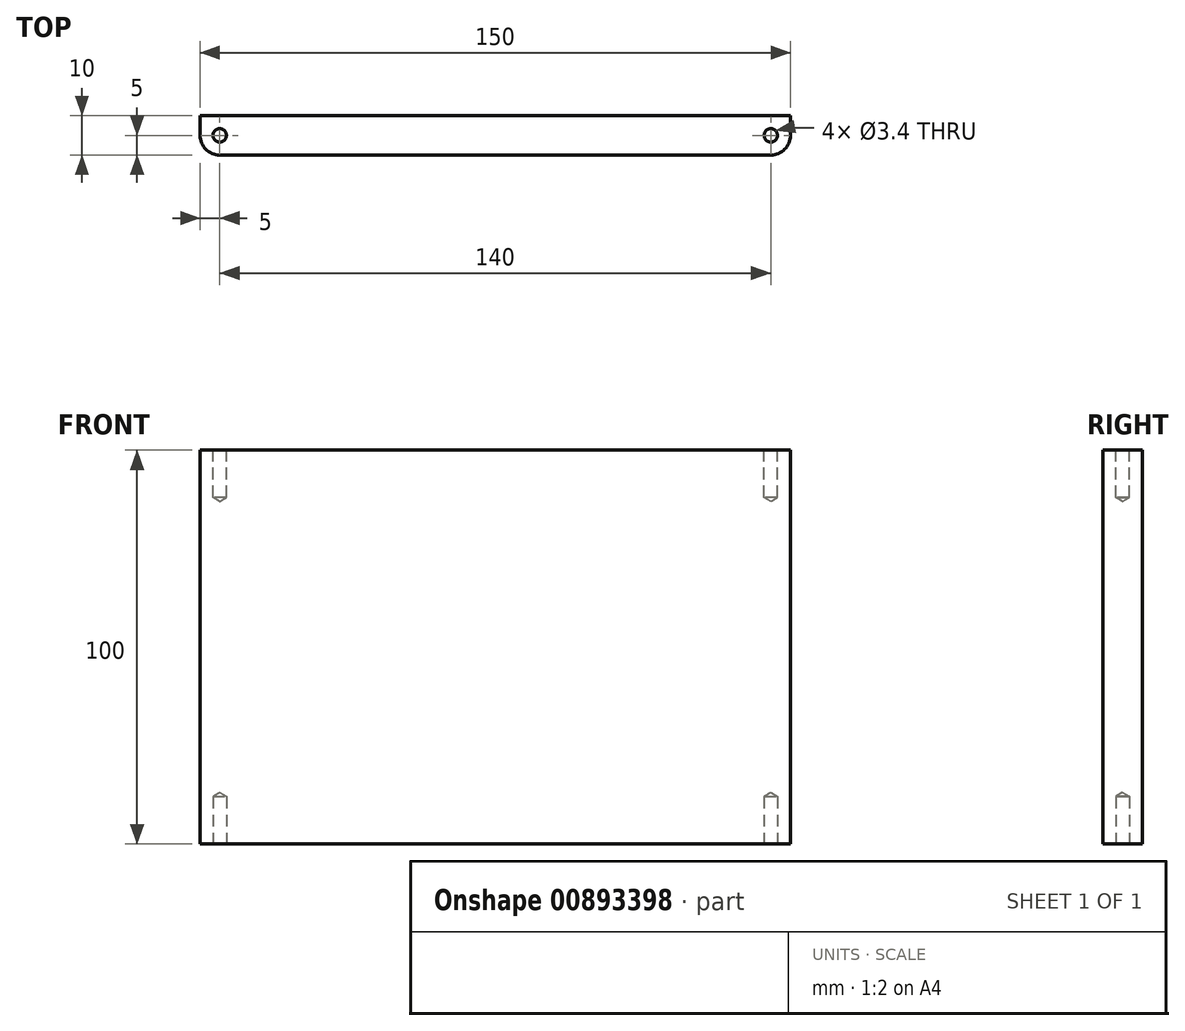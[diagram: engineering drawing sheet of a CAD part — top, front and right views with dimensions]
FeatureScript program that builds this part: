
annotation { "Feature Type Name" : "Feature", "Feature Type Description" : "" }
export const myFeature = defineFeature(function(context is Context, id is Id, definition is map)
    precondition{}
    {
        {
            var Q0;
            Q0=qCreatedBy(makeId("Front.planeOp"),FACE);
            var sketch = newSketch(context, id + "F0", { "sketchPlane" : qUnion([Q0])});
            skLineSegment(sketch, "E0.bottom", {"start": v(0, 0) * mm, "end": v(150, 0) * mm});
            skLineSegment(sketch, "E0.top", {"start": v(0, 100) * mm, "end": v(150, 100) * mm});
            skLineSegment(sketch, "E0.left", {"start": v(0, 0) * mm, "end": v(0, 100) * mm});
            skLineSegment(sketch, "E0.right", {"start": v(150, 0) * mm, "end": v(150, 100) * mm});
            skSolve(sketch);
        }
        {
            var Q0;
            Q0 = qSketchRegion(id + "F0", true);
            extrude(context, id + "F1", {"entities" : qUnion([Q0]), "depth" : 10 * mm, "offsetDistance" : 25 * mm});
        }
        {
            var Q0;
            Q0=makeQuery(id+"F1.opExtrude","SWEPT_FACE",FACE,{"disambiguationData":[OSD([sQuery(id+"F0.wireOp",EDGE,"E0.top")])]});
            var sketch = newSketch(context, id + "F2", { "sketchPlane" : qUnion([Q0])});
            skPoint(sketch, "E1", {"position": v(145, -5) * mm});
            skPoint(sketch, "E2", {"position": v(5, -5) * mm});
            skSolve(sketch);
        }
        {
            var Q0;
            Q0=sQuery(id+"F2.wireOp",VERTEX,"E1");
            var Q1;
            Q1=makeQuery(id+"F1.opExtrude","SWEPT_BODY",BODY,{"disambiguationData":[OSD([sQuery(id+"F0.wireOp",EDGE,"E0.bottom"),sQuery(id+"F0.wireOp",EDGE,"E0.top"),sQuery(id+"F0.wireOp",EDGE,"E0.left"),sQuery(id+"F0.wireOp",EDGE,"E0.right")])]});
            hole(context, id + "F3", {"style" : HoleStyle.SIMPLE, "endStyle" : HoleEndStyle.BLIND, "standardTappedOrClearance" : lookupTablePath({ "standard" : "ISO", "fit" : "Normal", "size" : "M3", "type" : "Clearance" }), "standardBlindInLast" : lookupTablePath({ "fit" : "Normal", "standard" : "ISO", "size" : "M3", "type" : "Clearance" }), "holeDiameter" : 3.4 * mm, "majorDiameter" : 5 * mm, "holeDepth" : 12 * mm, "isTappedThrough" : true, "tappedDepth" : 12 * mm, "tapClearance" : 3, "locations" : qUnion([Q0]), "scope" : qUnion([Q1])});
        }
        {
            var Q0;
            Q0=sQuery(id+"F2.wireOp",VERTEX,"E2");
            var Q1;
            Q1=makeQuery(id+"F1.opExtrude","SWEPT_BODY",BODY,{"disambiguationData":[OSD([sQuery(id+"F0.wireOp",EDGE,"E0.bottom"),sQuery(id+"F0.wireOp",EDGE,"E0.top"),sQuery(id+"F0.wireOp",EDGE,"E0.left"),sQuery(id+"F0.wireOp",EDGE,"E0.right")])]});
            hole(context, id + "F4", {"style" : HoleStyle.SIMPLE, "endStyle" : HoleEndStyle.BLIND, "standardTappedOrClearance" : lookupTablePath({ "standard" : "ISO", "fit" : "Normal", "size" : "M3", "type" : "Clearance" }), "standardBlindInLast" : lookupTablePath({ "fit" : "Normal", "standard" : "ISO", "size" : "M3", "type" : "Clearance" }), "holeDiameter" : 3.4 * mm, "majorDiameter" : 5 * mm, "holeDepth" : 12 * mm, "isTappedThrough" : true, "tappedDepth" : 12 * mm, "tapClearance" : 3, "locations" : qUnion([Q0]), "scope" : qUnion([Q1])});
        }
        {
            var Q0;
            Q0=makeQuery(id+"F1.opExtrude","SWEPT_FACE",FACE,{"disambiguationData":[OSD([sQuery(id+"F0.wireOp",EDGE,"E0.bottom")])]});
            var sketch = newSketch(context, id + "F5", { "sketchPlane" : qUnion([Q0])});
            skPoint(sketch, "E3", {"position": v(145, 5) * mm});
            skPoint(sketch, "E4", {"position": v(5, 5) * mm});
            skSolve(sketch);
        }
        {
            var Q0;
            Q0=sQuery(id+"F5.wireOp",VERTEX,"E3");
            var Q1;
            Q1=makeQuery(id+"F1.opExtrude","SWEPT_BODY",BODY,{"disambiguationData":[OSD([sQuery(id+"F0.wireOp",EDGE,"E0.bottom"),sQuery(id+"F0.wireOp",EDGE,"E0.top"),sQuery(id+"F0.wireOp",EDGE,"E0.left"),sQuery(id+"F0.wireOp",EDGE,"E0.right")])]});
            hole(context, id + "F6", {"style" : HoleStyle.SIMPLE, "endStyle" : HoleEndStyle.BLIND, "standardTappedOrClearance" : lookupTablePath({ "standard" : "ISO", "fit" : "Normal", "size" : "M3", "type" : "Clearance" }), "standardBlindInLast" : lookupTablePath({ "fit" : "Normal", "standard" : "ISO", "size" : "M3", "type" : "Clearance" }), "holeDiameter" : 3.4 * mm, "majorDiameter" : 5 * mm, "holeDepth" : 12 * mm, "isTappedThrough" : true, "tappedDepth" : 12 * mm, "tapClearance" : 3, "locations" : qUnion([Q0]), "scope" : qUnion([Q1])});
        }
        {
            var Q0;
            Q0=sQuery(id+"F5.wireOp",VERTEX,"E4");
            var Q1;
            Q1=makeQuery(id+"F1.opExtrude","SWEPT_BODY",BODY,{"disambiguationData":[OSD([sQuery(id+"F0.wireOp",EDGE,"E0.bottom"),sQuery(id+"F0.wireOp",EDGE,"E0.top"),sQuery(id+"F0.wireOp",EDGE,"E0.left"),sQuery(id+"F0.wireOp",EDGE,"E0.right")])]});
            hole(context, id + "F7", {"style" : HoleStyle.SIMPLE, "endStyle" : HoleEndStyle.BLIND, "standardTappedOrClearance" : lookupTablePath({ "standard" : "ISO", "fit" : "Normal", "size" : "M3", "type" : "Clearance" }), "standardBlindInLast" : lookupTablePath({ "fit" : "Normal", "standard" : "ISO", "size" : "M3", "type" : "Clearance" }), "holeDiameter" : 3.4 * mm, "majorDiameter" : 5 * mm, "holeDepth" : 12 * mm, "isTappedThrough" : true, "tappedDepth" : 12 * mm, "tapClearance" : 3, "locations" : qUnion([Q0]), "scope" : qUnion([Q1])});
        }
        {
            var Q0;
            Q0=makeQuery(id+"F1.opExtrude","CAP_EDGE",EDGE,{"disambiguationData":[OSD([sQuery(id+"F0.wireOp",EDGE,"E0.right")])],"isStart":false});
            fillet(context, id + "F8", {"entities" : qUnion([Q0]), "radius" : 5 * mm, "tangentPropagation" : true, "allowEdgeOverflow" : false});
        }
        {
            var Q0;
            Q0=makeQuery(id+"F1.opExtrude","CAP_EDGE",EDGE,{"disambiguationData":[OSD([sQuery(id+"F0.wireOp",EDGE,"E0.left")])],"isStart":false});
            fillet(context, id + "F9", {"entities" : qUnion([Q0]), "radius" : 5 * mm, "tangentPropagation" : true, "allowEdgeOverflow" : false});
        }
    });
